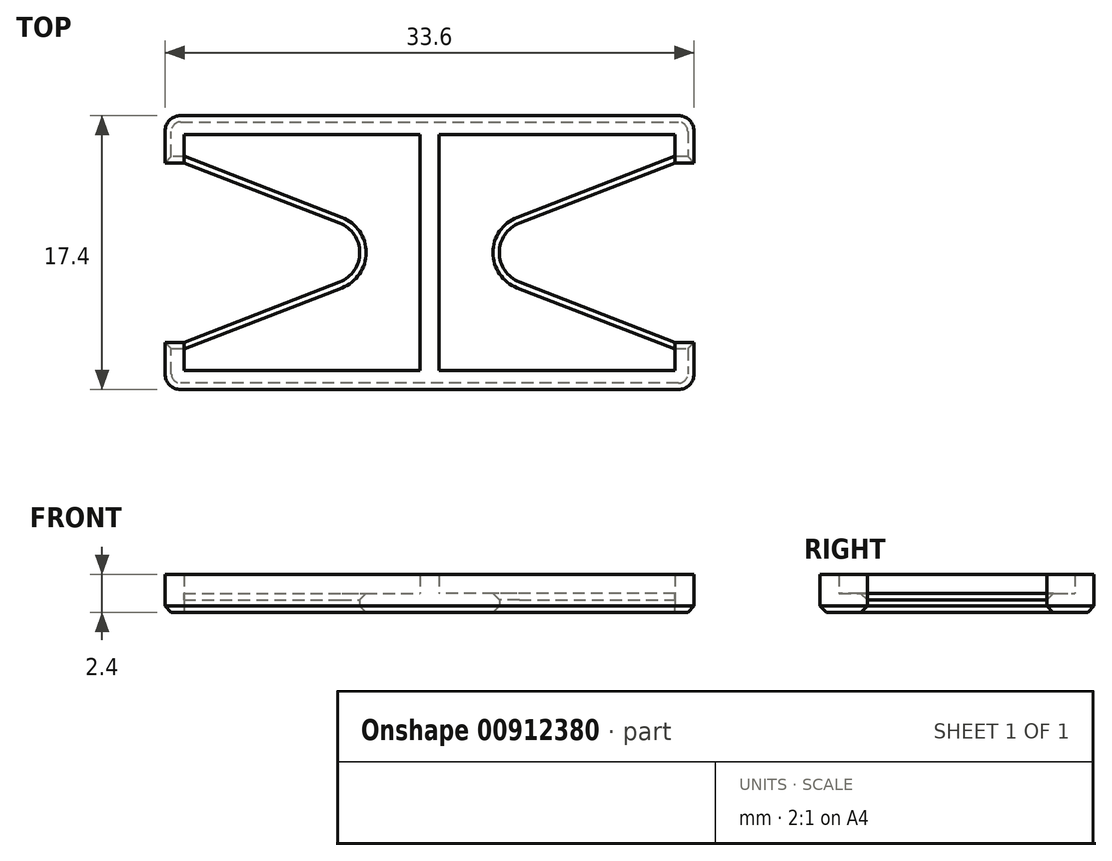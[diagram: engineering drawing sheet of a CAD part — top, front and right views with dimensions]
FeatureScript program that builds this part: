
annotation { "Feature Type Name" : "Feature", "Feature Type Description" : "" }
export const myFeature = defineFeature(function(context is Context, id is Id, definition is map)
    precondition{}
    {
        {
            assignVariable(context, id + "F0", {"name" : "wall", "anyValue" : 1.2});
        }
        {
            var Q0;
            Q0=qCreatedBy(makeId("Top.planeOp"),FACE);
            var sketch = newSketch(context, id + "F1", { "sketchPlane" : qUnion([Q0])});
            skLineSegment(sketch, "E0.bottom", {"start": v(-23.84, 17.7) * mm, "end": v(23.84, 17.7) * mm});
            skLineSegment(sketch, "E0.top", {"start": v(-23.84, -17.7) * mm, "end": v(23.84, -17.7) * mm});
            skLineSegment(sketch, "E0.left", {"start": v(-23.84, 17.7) * mm, "end": v(-23.84, -17.7) * mm});
            skLineSegment(sketch, "E0.right", {"start": v(23.84, 17.7) * mm, "end": v(23.84, -17.7) * mm});
            skLineSegment(sketch, "E1.bottom", {"start": v(-15.3, 7.2) * mm, "end": v(-0.9, 7.2) * mm, "construction": true});
            skLineSegment(sketch, "E1.top", {"start": v(-15.3, -7.2) * mm, "end": v(-0.9, -7.2) * mm, "construction": true});
            skLineSegment(sketch, "E1.left", {"start": v(-15.3, 7.2) * mm, "end": v(-15.3, -7.2) * mm, "construction": true});
            skLineSegment(sketch, "E1.right", {"start": v(-0.9, 7.2) * mm, "end": v(-0.9, -7.2) * mm, "construction": true});
            skLineSegment(sketch, "E2.bottom", {"start": v(0.9, 7.2) * mm, "end": v(15.3, 7.2) * mm, "construction": true});
            skLineSegment(sketch, "E2.top", {"start": v(0.9, -7.2) * mm, "end": v(15.3, -7.2) * mm, "construction": true});
            skLineSegment(sketch, "E2.left", {"start": v(0.9, 7.2) * mm, "end": v(0.9, -7.2) * mm, "construction": true});
            skLineSegment(sketch, "E2.right", {"start": v(15.3, 7.2) * mm, "end": v(15.3, -7.2) * mm, "construction": true});
            skPoint(sketch, "E3", {"position": v(0, 17.7) * mm});
            skPoint(sketch, "E4", {"position": v(23.84, 0) * mm});
            skLineSegment(sketch, "E5", {"start": v(-0.9, 0) * mm, "end": v(0.9, 0) * mm, "construction": true});
            skPoint(sketch, "E6", {"position": v(0, 0) * mm});
            skLineSegment(sketch, "E7", {"start": v(-16.8, 8.7) * mm, "end": v(-16.8, 5.7) * mm});
            skLineSegment(sketch, "E8", {"start": v(-15.6, 7.5) * mm, "end": v(-0.6, 7.5) * mm});
            skLineSegment(sketch, "E9", {"start": v(-0.6, 7.5) * mm, "end": v(-0.6, 0) * mm});
            skLineSegment(sketch, "E10", {"start": v(-16.8, 5.7) * mm, "end": v(-15.6, 5.7) * mm});
            skLineSegment(sketch, "E11", {"start": v(-15.6, 5.7) * mm, "end": v(-15.6, 7.5) * mm});
            skLineSegment(sketch, "E12", {"start": v(0, 0) * mm, "end": v(0, 8.7) * mm, "construction": true});
            skLineSegment(sketch, "E13", {"start": v(-16.8, 8.7) * mm, "end": v(0, 8.7) * mm});
            skLineSegment(sketch, "E14.MirrorCS", {"start": v(0.6, 7.5) * mm, "end": v(0.6, 0) * mm});
            skLineSegment(sketch, "E15.MirrorCS", {"start": v(15.6, 7.5) * mm, "end": v(0.6, 7.5) * mm});
            skLineSegment(sketch, "E16.MirrorCS", {"start": v(16.8, 8.7) * mm, "end": v(0, 8.7) * mm});
            skLineSegment(sketch, "E17.MirrorCS", {"start": v(16.8, 8.7) * mm, "end": v(16.8, 5.7) * mm});
            skLineSegment(sketch, "E18.MirrorCS", {"start": v(16.8, 5.7) * mm, "end": v(15.6, 5.7) * mm});
            skLineSegment(sketch, "E19.MirrorCS", {"start": v(15.6, 5.7) * mm, "end": v(15.6, 7.5) * mm});
            skLineSegment(sketch, "E20.MirrorCS", {"start": v(-0.6, -7.5) * mm, "end": v(-0.6, 0) * mm});
            skLineSegment(sketch, "E21.MirrorCS", {"start": v(-15.6, -7.5) * mm, "end": v(-0.6, -7.5) * mm});
            skLineSegment(sketch, "E22.MirrorCS", {"start": v(-15.6, -5.7) * mm, "end": v(-15.6, -7.5) * mm});
            skLineSegment(sketch, "E23.MirrorCS", {"start": v(-16.8, -5.7) * mm, "end": v(-15.6, -5.7) * mm});
            skLineSegment(sketch, "E24.MirrorCS", {"start": v(-16.8, -8.7) * mm, "end": v(-16.8, -5.7) * mm});
            skLineSegment(sketch, "E25.MirrorCS", {"start": v(-16.8, -8.7) * mm, "end": v(0, -8.7) * mm});
            skLineSegment(sketch, "E26.MirrorCS", {"start": v(16.8, -8.7) * mm, "end": v(0, -8.7) * mm});
            skLineSegment(sketch, "E27.MirrorCS", {"start": v(16.8, -8.7) * mm, "end": v(16.8, -5.7) * mm});
            skLineSegment(sketch, "E28.MirrorCS", {"start": v(16.8, -5.7) * mm, "end": v(15.6, -5.7) * mm});
            skLineSegment(sketch, "E29.MirrorCS", {"start": v(15.6, -5.7) * mm, "end": v(15.6, -7.5) * mm});
            skLineSegment(sketch, "E30.MirrorCS", {"start": v(15.6, -7.5) * mm, "end": v(0.6, -7.5) * mm});
            skLineSegment(sketch, "E31.MirrorCS", {"start": v(0.6, -7.5) * mm, "end": v(0.6, 0) * mm});
            skLineSegment(sketch, "E32", {"start": v(-15.6, -5.7) * mm, "end": v(-0.9, 0) * mm});
            skLineSegment(sketch, "E33", {"start": v(-15.6, 5.7) * mm, "end": v(-0.9, 0) * mm});
            skLineSegment(sketch, "E34", {"start": v(15.6, 5.7) * mm, "end": v(0.9, 0) * mm});
            skLineSegment(sketch, "E35", {"start": v(15.6, -5.7) * mm, "end": v(0.9, 0) * mm});
            skSolve(sketch);
        }
        {
            var Q0;
            Q0=makeQuery(id+"F1.imprint","IMPRINT",FACE,{"disambiguationData":[TD([[makeQuery(id+"F1.imprint","IMPRINT",EDGE,{"derivedFrom":sQuery(id+"F1.wireOp",EDGE,"E8")}),-1.0]])]});
            var Q1;
            Q1=makeQuery(id+"F1.imprint","IMPRINT",FACE,{"disambiguationData":[TD([[makeQuery(id+"F1.imprint","IMPRINT",EDGE,{"derivedFrom":sQuery(id+"F1.wireOp",EDGE,"E14.MirrorCS")}),1.0]])]});
            extrude(context, id + "F2", {"entities" : qUnion([Q0, Q1]), "depth" : (getVariable(context, 'wall')) * mm, "offsetDistance" : 25 * mm});
        }
        {
            var Q0;
            Q0=makeQuery(id+"F1.imprint","IMPRINT",FACE,{"disambiguationData":[TD([[makeQuery(id+"F1.imprint","IMPRINT",EDGE,{"derivedFrom":sQuery(id+"F1.wireOp",EDGE,"E7")}),1.0]])]});
            extrude(context, id + "F3", {"entities" : qUnion([Q0]), "operationType" : NewBodyOperationType.ADD, "depth" : (getVariable(context, 'wall') * 2) * mm, "offsetDistance" : 25 * mm});
        }
        {
            var Q0;
            Q0=makeQuery(id+"F2.opExtrude","SWEPT_EDGE",EDGE,{"disambiguationData":[OSD([sQuery(id+"F1.wireOp",EDGE,"E32"),sQuery(id+"F1.wireOp",EDGE,"E33")])]});
            var Q1;
            Q1=makeQuery(id+"F2.opExtrude","SWEPT_EDGE",EDGE,{"disambiguationData":[OSD([sQuery(id+"F1.wireOp",EDGE,"E34"),sQuery(id+"F1.wireOp",EDGE,"E35")])]});
            fillet(context, id + "F4", {"entities" : qUnion([Q0, Q1]), "radius" : 2 * mm, "tangentPropagation" : true, "allowEdgeOverflow" : false});
        }
        {
            var Q0;
            Q0=makeQuery(id+"F3.opExtrude","SWEPT_EDGE",EDGE,{"disambiguationData":[OSD([sQuery(id+"F1.wireOp",EDGE,"E26.MirrorCS"),sQuery(id+"F1.wireOp",EDGE,"E27.MirrorCS")])]});
            var Q1;
            Q1=makeQuery(id+"F3.opExtrude","SWEPT_EDGE",EDGE,{"disambiguationData":[OSD([sQuery(id+"F1.wireOp",EDGE,"E16.MirrorCS"),sQuery(id+"F1.wireOp",EDGE,"E17.MirrorCS")])]});
            var Q2;
            Q2=makeQuery(id+"F3.opExtrude","SWEPT_EDGE",EDGE,{"disambiguationData":[OSD([sQuery(id+"F1.wireOp",EDGE,"E24.MirrorCS"),sQuery(id+"F1.wireOp",EDGE,"E25.MirrorCS")])]});
            var Q3;
            Q3=makeQuery(id+"F3.opExtrude","SWEPT_EDGE",EDGE,{"disambiguationData":[OSD([sQuery(id+"F1.wireOp",EDGE,"E7"),sQuery(id+"F1.wireOp",EDGE,"E13")])]});
            fillet(context, id + "F5", {"entities" : qUnion([Q0, Q1, Q2, Q3]), "radius" : 1 * mm, "tangentPropagation" : true, "allowEdgeOverflow" : false});
        }
        {
            var Q0;
            {var subQ0=sQuery(id+"F1.wireOp",EDGE,"E31.MirrorCS");var subQ1=sQuery(id+"F1.wireOp",EDGE,"E30.MirrorCS");var subQ2=sQuery(id+"F1.wireOp",EDGE,"E29.MirrorCS");var subQ3=sQuery(id+"F1.wireOp",EDGE,"E22.MirrorCS");var subQ4=sQuery(id+"F1.wireOp",EDGE,"E21.MirrorCS");var subQ5=sQuery(id+"F1.wireOp",EDGE,"E20.MirrorCS");var subQ6=sQuery(id+"F1.wireOp",EDGE,"E19.MirrorCS");var subQ7=sQuery(id+"F1.wireOp",EDGE,"E15.MirrorCS");var subQ8=sQuery(id+"F1.wireOp",EDGE,"E14.MirrorCS");var subQ9=sQuery(id+"F1.wireOp",EDGE,"E11");var subQ10=sQuery(id+"F1.wireOp",EDGE,"E9");var subQ11=sQuery(id+"F1.wireOp",EDGE,"E8");Q0=makeQuery(id+"F3.boolean.opBoolean","MERGE",FACE,{"derivedFrom":[makeQuery(id+"F2.opExtrude","CAP_FACE",FACE,{"disambiguationData":[OSD([subQ11,subQ10,subQ9,subQ5,subQ4,subQ3,sQuery(id+"F1.wireOp",EDGE,"E32"),sQuery(id+"F1.wireOp",EDGE,"E33")])],"isStart":true}),makeQuery(id+"F2.opExtrude","CAP_FACE",FACE,{"disambiguationData":[OSD([subQ8,subQ7,subQ6,subQ2,subQ1,subQ0,sQuery(id+"F1.wireOp",EDGE,"E34"),sQuery(id+"F1.wireOp",EDGE,"E35")])],"isStart":true}),makeQuery(id+"F3.opExtrude","CAP_FACE",FACE,{"disambiguationData":[OSD([sQuery(id+"F1.wireOp",EDGE,"E7"),subQ11,subQ10,sQuery(id+"F1.wireOp",EDGE,"E10"),subQ9,sQuery(id+"F1.wireOp",EDGE,"E13"),subQ8,subQ7,sQuery(id+"F1.wireOp",EDGE,"E16.MirrorCS"),sQuery(id+"F1.wireOp",EDGE,"E17.MirrorCS"),sQuery(id+"F1.wireOp",EDGE,"E18.MirrorCS"),subQ6,subQ5,subQ4,subQ3,sQuery(id+"F1.wireOp",EDGE,"E23.MirrorCS"),sQuery(id+"F1.wireOp",EDGE,"E24.MirrorCS"),sQuery(id+"F1.wireOp",EDGE,"E25.MirrorCS"),sQuery(id+"F1.wireOp",EDGE,"E26.MirrorCS"),sQuery(id+"F1.wireOp",EDGE,"E27.MirrorCS"),sQuery(id+"F1.wireOp",EDGE,"E28.MirrorCS"),subQ2,subQ1,subQ0])],"isStart":true})]});}
            var Q1;
            Q1=makeQuery(id+"F2.opExtrude","CAP_EDGE",EDGE,{"disambiguationData":[OSD([sQuery(id+"F1.wireOp",EDGE,"E32")])],"isStart":false});
            var Q2;
            {var subQ0=sQuery(id+"F1.wireOp",EDGE,"E35");var subQ1=sQuery(id+"F1.wireOp",EDGE,"E34");Q2=makeQuery(id+"F4.opFillet","BLEND_EDGE",EDGE,{"blendedFrom":[makeQuery(id+"F2.opExtrude","SWEPT_EDGE",EDGE,{"disambiguationData":[OSD([subQ1,subQ0])]}),makeQuery(id+"F2.opExtrude","CAP_FACE",FACE,{"disambiguationData":[OSD([sQuery(id+"F1.wireOp",EDGE,"E14.MirrorCS"),sQuery(id+"F1.wireOp",EDGE,"E15.MirrorCS"),sQuery(id+"F1.wireOp",EDGE,"E19.MirrorCS"),sQuery(id+"F1.wireOp",EDGE,"E29.MirrorCS"),sQuery(id+"F1.wireOp",EDGE,"E30.MirrorCS"),sQuery(id+"F1.wireOp",EDGE,"E31.MirrorCS"),subQ1,subQ0])],"isStart":false})],"blendedInto":[makeQuery(id+"F2.opExtrude","CAP_FACE",FACE,{"disambiguationData":[OSD([sQuery(id+"F1.wireOp",EDGE,"E14.MirrorCS"),sQuery(id+"F1.wireOp",EDGE,"E15.MirrorCS"),sQuery(id+"F1.wireOp",EDGE,"E19.MirrorCS"),sQuery(id+"F1.wireOp",EDGE,"E29.MirrorCS"),sQuery(id+"F1.wireOp",EDGE,"E30.MirrorCS"),sQuery(id+"F1.wireOp",EDGE,"E31.MirrorCS"),subQ1,subQ0])],"isStart":false})]});}
            chamfer(context, id + "F6", {"entities" : qUnion([Q0, Q1, Q2]), "width" : 0.4 * mm, "tangentPropagation" : true});
        }
    });
